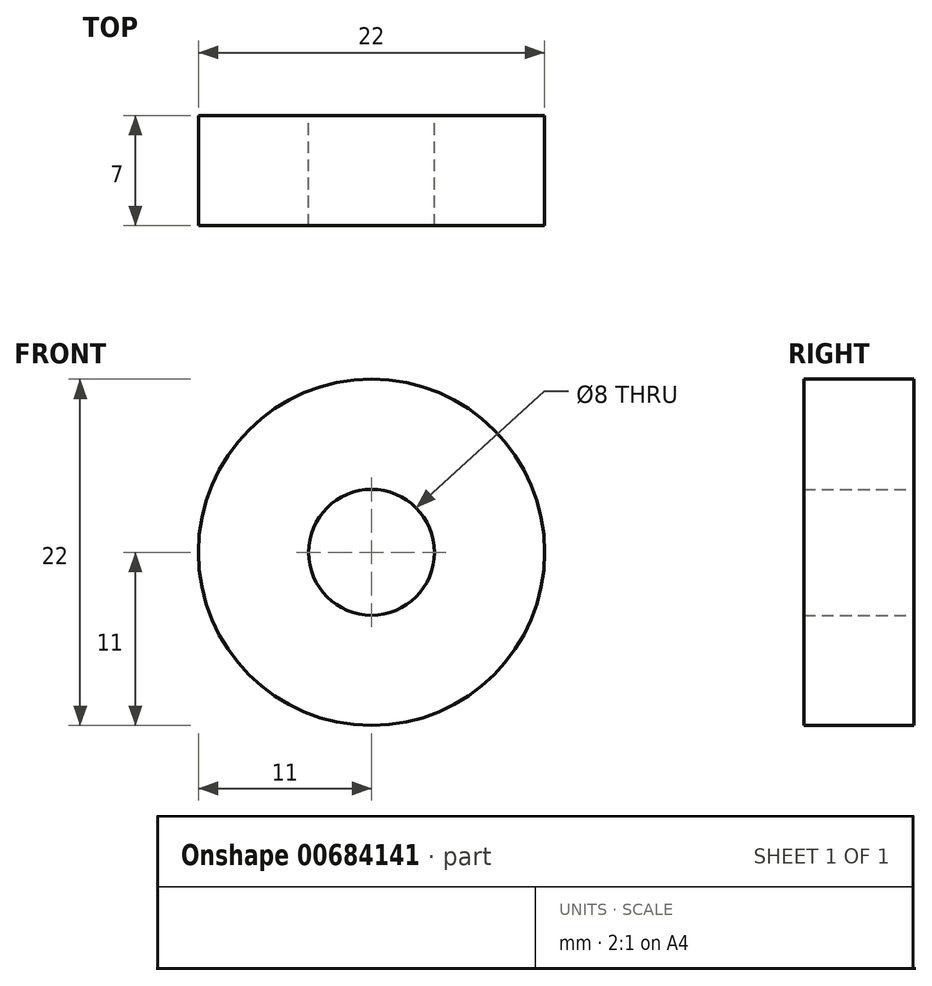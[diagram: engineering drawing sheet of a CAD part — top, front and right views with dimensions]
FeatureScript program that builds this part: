
annotation { "Feature Type Name" : "Feature", "Feature Type Description" : "" }
export const myFeature = defineFeature(function(context is Context, id is Id, definition is map)
    precondition{}
    {
        {
            var Q0;
            Q0=qCreatedBy(makeId("Front.planeOp"),FACE);
            var sketch = newSketch(context, id + "F0", { "sketchPlane" : qUnion([Q0])});
            skCircle(sketch, "E0", {"center": v(0, 0) * mm, "radius": 4 * mm});
            skCircle(sketch, "E1", {"center": v(0, 0) * mm, "radius": 11 * mm});
            skSolve(sketch);
        }
        {
            var Q0;
            Q0 = qSketchRegion(id + "F0", true);
            extrude(context, id + "F1", {"entities" : qUnion([Q0]), "depth" : 7 * mm, "offsetDistance" : 25 * mm});
        }
    });
